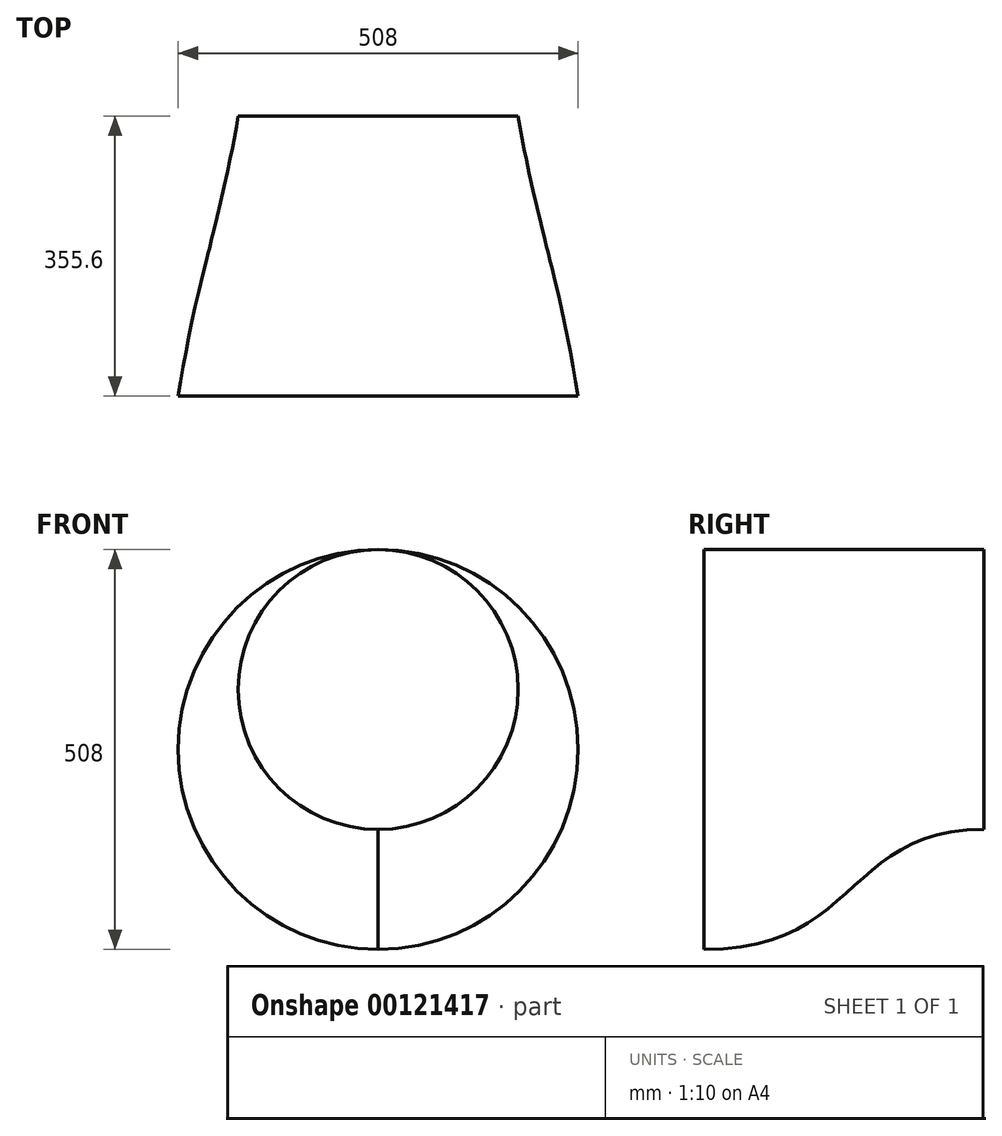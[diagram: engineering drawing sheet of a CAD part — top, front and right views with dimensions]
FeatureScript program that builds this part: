
annotation { "Feature Type Name" : "Feature", "Feature Type Description" : "" }
export const myFeature = defineFeature(function(context is Context, id is Id, definition is map)
    precondition{}
    {
        {
            var Q0;
            Q0=qCreatedBy(makeId("Front.planeOp"),FACE);
            var sketch = newSketch(context, id + "F0", { "sketchPlane" : qUnion([Q0])});
            skCircle(sketch, "E0", {"center": v(0, 0) * mm, "radius": 177.8 * mm});
            skSolve(sketch);
        }
        {
            var Q0;
            Q0=makeQuery(id+"F0.imprint","IMPRINT",FACE,{"disambiguationData":[TD([[makeQuery(id+"F0.imprint","IMPRINT",EDGE,{"derivedFrom":sQuery(id+"F0.wireOp",EDGE,"E0")}),1.0]])]});
            cPlane(context, id + "F1", {"entities" : qUnion([Q0]), "cplaneType" : CPlaneType.OFFSET, "offset" : 355.6 * mm, "width" : 152.4 * mm, "height" : 152.4 * mm});
        }
        {
            var Q0;
            Q0=qCreatedBy(makeId("Right.planeOp"),FACE);
            var sketch = newSketch(context, id + "F2", { "sketchPlane" : qUnion([Q0])});
            skLineSegment(sketch, "E1", {"start": v(0, 177.8) * mm, "end": v(-355.6, 177.8) * mm});
            skLineSegment(sketch, "E2", {"start": v(0, 177.8) * mm, "end": v(0, -177.8) * mm});
            skLineSegment(sketch, "E3", {"start": v(-355.6, -330.2) * mm, "end": v(-355.6, 177.8) * mm});
            skFitSpline(sketch, "E4", {"points": [v(0, -177.8) * mm, v(-355.6, -330.2) * mm], "startDerivative": vector(-529.68, 0) * mm, "endDerivative": vector(-593.43, 0) * mm});
            skPoint(sketch, "E5", {"position": v(-12.7, -178.07) * mm});
            skPoint(sketch, "E6", {"position": v(-25.4, -178.94) * mm});
            skPoint(sketch, "E7", {"position": v(-38.1, -180.46) * mm});
            skPoint(sketch, "E8", {"position": v(-50.8, -182.73) * mm});
            skPoint(sketch, "E9", {"position": v(-63.5, -185.84) * mm});
            skPoint(sketch, "E10", {"position": v(-76.2, -189.9) * mm});
            skPoint(sketch, "E11", {"position": v(-88.89, -195) * mm});
            skPoint(sketch, "E12", {"position": v(-101.58, -201.26) * mm});
            skPoint(sketch, "E13", {"position": v(-114.26, -208.75) * mm});
            skPoint(sketch, "E14", {"position": v(-126.95, -217.49) * mm});
            skPoint(sketch, "E15", {"position": v(-139.62, -227.39) * mm});
            skPoint(sketch, "E16", {"position": v(-152.3, -238.22) * mm});
            skPoint(sketch, "E17", {"position": v(-164.97, -249.6) * mm});
            skPoint(sketch, "E18", {"position": v(-177.66, -261.03) * mm});
            skPoint(sketch, "E19", {"position": v(-190.35, -272.04) * mm});
            skPoint(sketch, "E20", {"position": v(-203.05, -282.24) * mm});
            skPoint(sketch, "E21", {"position": v(-215.76, -291.4) * mm});
            skPoint(sketch, "E22", {"position": v(-228.48, -299.4) * mm});
            skPoint(sketch, "E23", {"position": v(-241.2, -306.28) * mm});
            skPoint(sketch, "E24", {"position": v(-253.92, -312.08) * mm});
            skPoint(sketch, "E25", {"position": v(-266.64, -316.9) * mm});
            skPoint(sketch, "E26", {"position": v(-279.36, -320.82) * mm});
            skPoint(sketch, "E27", {"position": v(-292.07, -323.94) * mm});
            skPoint(sketch, "E28", {"position": v(-304.78, -326.34) * mm});
            skPoint(sketch, "E29", {"position": v(-317.5, -328.1) * mm});
            skPoint(sketch, "E30", {"position": v(-330.2, -329.3) * mm});
            skPoint(sketch, "E31", {"position": v(-342.9, -329.98) * mm});
            skLineSegment(sketch, "E32", {"start": v(-342.9, -329.98) * mm, "end": v(-343.29, 177.8) * mm});
            skLineSegment(sketch, "E33", {"start": v(-330.2, -329.3) * mm, "end": v(-330.59, 177.8) * mm});
            skLineSegment(sketch, "E34", {"start": v(-317.5, -328.1) * mm, "end": v(-317.5, 177.8) * mm});
            skLineSegment(sketch, "E35", {"start": v(-304.78, -326.34) * mm, "end": v(-305.19, 177.8) * mm});
            skLineSegment(sketch, "E36", {"start": v(-292.07, -323.94) * mm, "end": v(-292.07, 177.8) * mm});
            skLineSegment(sketch, "E37", {"start": v(-279.36, -320.82) * mm, "end": v(-279.36, 177.8) * mm});
            skLineSegment(sketch, "E38", {"start": v(-266.64, -316.9) * mm, "end": v(-266.64, 177.8) * mm});
            skLineSegment(sketch, "E39", {"start": v(-253.92, -312.08) * mm, "end": v(-253.92, 177.8) * mm});
            skLineSegment(sketch, "E40", {"start": v(-241.2, -306.28) * mm, "end": v(-241.2, 177.8) * mm});
            skLineSegment(sketch, "E41", {"start": v(-228.48, -299.4) * mm, "end": v(-228.48, 177.8) * mm});
            skLineSegment(sketch, "E42", {"start": v(-215.76, -291.4) * mm, "end": v(-216.26, 177.8) * mm});
            skLineSegment(sketch, "E43", {"start": v(-203.05, -282.24) * mm, "end": v(-203.55, 177.8) * mm});
            skLineSegment(sketch, "E44", {"start": v(-190.35, -272.04) * mm, "end": v(-190.35, 177.8) * mm});
            skLineSegment(sketch, "E45", {"start": v(-177.66, -261.03) * mm, "end": v(-177.66, 177.8) * mm});
            skLineSegment(sketch, "E46", {"start": v(-164.97, -249.6) * mm, "end": v(-164.97, 177.8) * mm});
            skLineSegment(sketch, "E47", {"start": v(-152.3, -238.22) * mm, "end": v(-152.3, 177.8) * mm});
            skLineSegment(sketch, "E48", {"start": v(-139.62, -227.39) * mm, "end": v(-139.62, 177.8) * mm});
            skLineSegment(sketch, "E49", {"start": v(-126.95, -217.49) * mm, "end": v(-127.3, 177.8) * mm});
            skLineSegment(sketch, "E50", {"start": v(-114.26, -208.75) * mm, "end": v(-114.61, 177.8) * mm});
            skLineSegment(sketch, "E51", {"start": v(-101.58, -201.26) * mm, "end": v(-101.92, 177.8) * mm});
            skLineSegment(sketch, "E52", {"start": v(-88.89, -195) * mm, "end": v(-89.23, 177.8) * mm});
            skLineSegment(sketch, "E53", {"start": v(-76.2, -189.9) * mm, "end": v(-76.53, 177.8) * mm});
            skLineSegment(sketch, "E54", {"start": v(-63.5, -185.84) * mm, "end": v(-63.83, 177.8) * mm});
            skLineSegment(sketch, "E55", {"start": v(-50.8, -182.73) * mm, "end": v(-51.13, 177.8) * mm});
            skLineSegment(sketch, "E56", {"start": v(-38.1, -180.46) * mm, "end": v(-38.37, 177.8) * mm});
            skLineSegment(sketch, "E57", {"start": v(-25.4, -178.94) * mm, "end": v(-25.4, 177.8) * mm});
            skLineSegment(sketch, "E58", {"start": v(-12.7, -178.07) * mm, "end": v(-12.7, 177.8) * mm});
            skPoint(sketch, "E59", {"position": v(-12.7, -0.14) * mm});
            skPoint(sketch, "E60", {"position": v(-25.4, -0.57) * mm});
            skPoint(sketch, "E61", {"position": v(-38.24, -1.33) * mm});
            skPoint(sketch, "E62", {"position": v(-50.96, -2.46) * mm});
            skPoint(sketch, "E63", {"position": v(-63.66, -4.02) * mm});
            skPoint(sketch, "E64", {"position": v(-76.36, -6.05) * mm});
            skPoint(sketch, "E65", {"position": v(-89.06, -8.6) * mm});
            skPoint(sketch, "E66", {"position": v(-101.75, -11.73) * mm});
            skPoint(sketch, "E67", {"position": v(-114.44, -15.47) * mm});
            skPoint(sketch, "E68", {"position": v(-127.12, -19.84) * mm});
            skPoint(sketch, "E69", {"position": v(-139.62, -24.8) * mm});
            skPoint(sketch, "E70", {"position": v(-152.3, -30.21) * mm});
            skPoint(sketch, "E71", {"position": v(-164.97, -35.9) * mm});
            skPoint(sketch, "E72", {"position": v(-177.66, -41.62) * mm});
            skPoint(sketch, "E73", {"position": v(-190.35, -47.12) * mm});
            skPoint(sketch, "E74", {"position": v(-203.3, -52.22) * mm});
            skPoint(sketch, "E75", {"position": v(-216, -56.8) * mm});
            skPoint(sketch, "E76", {"position": v(-228.48, -60.8) * mm});
            skPoint(sketch, "E77", {"position": v(-241.2, -64.24) * mm});
            skPoint(sketch, "E78", {"position": v(-253.92, -67.14) * mm});
            skPoint(sketch, "E79", {"position": v(-266.64, -69.55) * mm});
            skPoint(sketch, "E80", {"position": v(-279.36, -71.5) * mm});
            skPoint(sketch, "E81", {"position": v(-292.07, -73.07) * mm});
            skPoint(sketch, "E82", {"position": v(-304.99, -74.27) * mm});
            skPoint(sketch, "E83", {"position": v(-317.5, -75.15) * mm});
            skPoint(sketch, "E84", {"position": v(-330.4, -75.75) * mm});
            skPoint(sketch, "E85", {"position": v(-343.1, -76.1) * mm});
            skPoint(sketch, "E86", {"position": v(-356.2, -76.1) * mm});
            skLineSegment(sketch, "E87", {"start": v(-356.2, -76.1) * mm, "end": v(-369.14, -76.1) * mm});
            skLineSegment(sketch, "E88", {"start": v(-343.1, -76.1) * mm, "end": v(-352.35, -75.75) * mm});
            skLineSegment(sketch, "E89", {"start": v(-330.4, -75.75) * mm, "end": v(-338.74, -75.76) * mm});
            skLineSegment(sketch, "E90", {"start": v(-317.5, -75.15) * mm, "end": v(-325.12, -75.15) * mm});
            skLineSegment(sketch, "E91", {"start": v(-304.99, -74.27) * mm, "end": v(-311.06, -74.27) * mm});
            skLineSegment(sketch, "E92", {"start": v(-292.07, -73.07) * mm, "end": v(-298.8, -73.07) * mm});
            skLineSegment(sketch, "E93", {"start": v(-279.36, -71.5) * mm, "end": v(-287.43, -71.5) * mm});
            skLineSegment(sketch, "E94", {"start": v(-266.64, -69.55) * mm, "end": v(-274.71, -69.55) * mm});
            skLineSegment(sketch, "E95", {"start": v(-253.92, -67.14) * mm, "end": v(-261.99, -67.14) * mm});
            skLineSegment(sketch, "E96", {"start": v(-241.2, -64.24) * mm, "end": v(-250.17, -64.24) * mm});
            skLineSegment(sketch, "E97", {"start": v(-228.48, -60.8) * mm, "end": v(-236.54, -60.8) * mm});
            skLineSegment(sketch, "E98", {"start": v(-216, -56.8) * mm, "end": v(-223.43, -56.8) * mm});
            skLineSegment(sketch, "E99", {"start": v(-203.3, -52.22) * mm, "end": v(-211.63, -52.22) * mm});
            skLineSegment(sketch, "E100", {"start": v(-190.35, -47.12) * mm, "end": v(-198.29, -47.12) * mm});
            skLineSegment(sketch, "E101", {"start": v(-177.66, -41.62) * mm, "end": v(-186.05, -41.62) * mm});
            skLineSegment(sketch, "E102", {"start": v(-164.97, -35.9) * mm, "end": v(-173.1, -35.9) * mm});
            skLineSegment(sketch, "E103", {"start": v(-152.3, -30.21) * mm, "end": v(-159.44, -30.21) * mm});
            skLineSegment(sketch, "E104", {"start": v(-139.62, -24.8) * mm, "end": v(-146.5, -24.8) * mm});
            skLineSegment(sketch, "E105", {"start": v(-127.12, -19.84) * mm, "end": v(-135.03, -19.85) * mm});
            skLineSegment(sketch, "E106", {"start": v(-114.44, -15.47) * mm, "end": v(-122.8, -15.48) * mm});
            skLineSegment(sketch, "E107", {"start": v(-101.75, -11.73) * mm, "end": v(-109.5, -11.74) * mm});
            skLineSegment(sketch, "E108", {"start": v(-89.06, -8.6) * mm, "end": v(-96.54, -8.6) * mm});
            skLineSegment(sketch, "E109", {"start": v(-76.36, -6.05) * mm, "end": v(-84.66, -6.05) * mm});
            skLineSegment(sketch, "E110", {"start": v(-63.66, -4.02) * mm, "end": v(-72.06, -4.02) * mm});
            skLineSegment(sketch, "E111", {"start": v(-50.96, -2.46) * mm, "end": v(-57.66, -2.46) * mm});
            skLineSegment(sketch, "E112", {"start": v(-38.24, -1.33) * mm, "end": v(-45.75, -1.33) * mm});
            skLineSegment(sketch, "E113", {"start": v(-25.4, -0.57) * mm, "end": v(-33.69, -0.57) * mm});
            skLineSegment(sketch, "E114", {"start": v(-12.7, -0.14) * mm, "end": v(-19.46, -0.14) * mm});
            skLineSegment(sketch, "E115", {"start": v(0, 0) * mm, "end": v(-5.96, 0) * mm});
            skLineSegment(sketch, "E116", {"start": v(-1093.74, 163.5) * mm, "end": v(-1093.74, -355.24) * mm});
            skLineSegment(sketch, "E117", {"start": v(-1171.66, -95.87) * mm, "end": v(-1295.5, -95.87) * mm});
            skSolve(sketch);
        }
        {
            var Q0;
            Q0=qCreatedBy(id+"F1.planeOp",FACE);
            var sketch = newSketch(context, id + "F3", { "sketchPlane" : qUnion([Q0])});
            skCircle(sketch, "E118", {"center": v(0, -76.2) * mm, "radius": 254 * mm});
            skLineSegment(sketch, "E119", {"start": v(0, -330.2) * mm, "end": v(0, 177.8) * mm});
            skSolve(sketch);
        }
        {
            var Q0;
            Q0=makeQuery(id+"F0.imprint","IMPRINT",FACE,{"disambiguationData":[TD([[makeQuery(id+"F0.imprint","IMPRINT",EDGE,{"derivedFrom":sQuery(id+"F0.wireOp",EDGE,"E0")}),1.0]])]});
            cPlane(context, id + "F4", {"entities" : qUnion([Q0]), "cplaneType" : CPlaneType.OFFSET, "offset" : 12.7 * mm, "width" : 152.4 * mm, "height" : 152.4 * mm});
        }
        {
            var Q0;
            Q0=makeQuery(id+"F0.imprint","IMPRINT",FACE,{"disambiguationData":[TD([[makeQuery(id+"F0.imprint","IMPRINT",EDGE,{"derivedFrom":sQuery(id+"F0.wireOp",EDGE,"E0")}),1.0]])]});
            cPlane(context, id + "F5", {"entities" : qUnion([Q0]), "cplaneType" : CPlaneType.OFFSET, "offset" : 25.4 * mm, "width" : 152.4 * mm, "height" : 152.4 * mm});
        }
        {
            var Q0;
            Q0=makeQuery(id+"F0.imprint","IMPRINT",FACE,{"disambiguationData":[TD([[makeQuery(id+"F0.imprint","IMPRINT",EDGE,{"derivedFrom":sQuery(id+"F0.wireOp",EDGE,"E0")}),1.0]])]});
            cPlane(context, id + "F6", {"entities" : qUnion([Q0]), "cplaneType" : CPlaneType.OFFSET, "offset" : 38.1 * mm, "width" : 152.4 * mm, "height" : 152.4 * mm});
        }
        {
            var Q0;
            Q0=makeQuery(id+"F0.imprint","IMPRINT",FACE,{"disambiguationData":[TD([[makeQuery(id+"F0.imprint","IMPRINT",EDGE,{"derivedFrom":sQuery(id+"F0.wireOp",EDGE,"E0")}),1.0]])]});
            cPlane(context, id + "F7", {"entities" : qUnion([Q0]), "cplaneType" : CPlaneType.OFFSET, "offset" : 50.8 * mm, "width" : 152.4 * mm, "height" : 152.4 * mm});
        }
        {
            var Q0;
            Q0=makeQuery(id+"F0.imprint","IMPRINT",FACE,{"disambiguationData":[TD([[makeQuery(id+"F0.imprint","IMPRINT",EDGE,{"derivedFrom":sQuery(id+"F0.wireOp",EDGE,"E0")}),1.0]])]});
            cPlane(context, id + "F8", {"entities" : qUnion([Q0]), "cplaneType" : CPlaneType.OFFSET, "offset" : 63.5 * mm, "width" : 152.4 * mm, "height" : 152.4 * mm});
        }
        {
            var Q0;
            Q0=makeQuery(id+"F3.imprint","IMPRINT",FACE,{"disambiguationData":[TD([[makeQuery(id+"F3.imprint","IMPRINT",EDGE,{"derivedFrom":sQuery(id+"F3.wireOp",EDGE,"E118")}),1.0]])]});
            var Q1;
            Q1=sQuery(id+"F0.wireOp",EDGE,"E0");
            var Q2;
            Q2=sQuery(id+"F3.wireOp",EDGE,"E118");
            var Q3;
            Q3=sQuery(id+"F2.wireOp",EDGE,"E4");
            var Q4;
            Q4=sQuery(id+"F2.wireOp",EDGE,"E1");
            loft(context, id + "F9", {"bodyType" : ToolBodyType.SURFACE, "addGuides" : true, "sheetProfilesArray" : [{ "sheetProfileEntities" : qUnion([Q0]) }], "wireProfilesArray" : [{ "wireProfileEntities" : qUnion([Q1]) }, { "wireProfileEntities" : qUnion([Q2]) }], "guidesArray" : [{ "guideEntities" : qUnion([Q3]), "guideDerivativeType" : LoftGuideDerivativeType.DEFAULT, "guideDerivativeMagnitude" : 1 }, { "guideEntities" : qUnion([Q4]), "guideDerivativeType" : LoftGuideDerivativeType.DEFAULT, "guideDerivativeMagnitude" : 1 }]});
        }
    });
